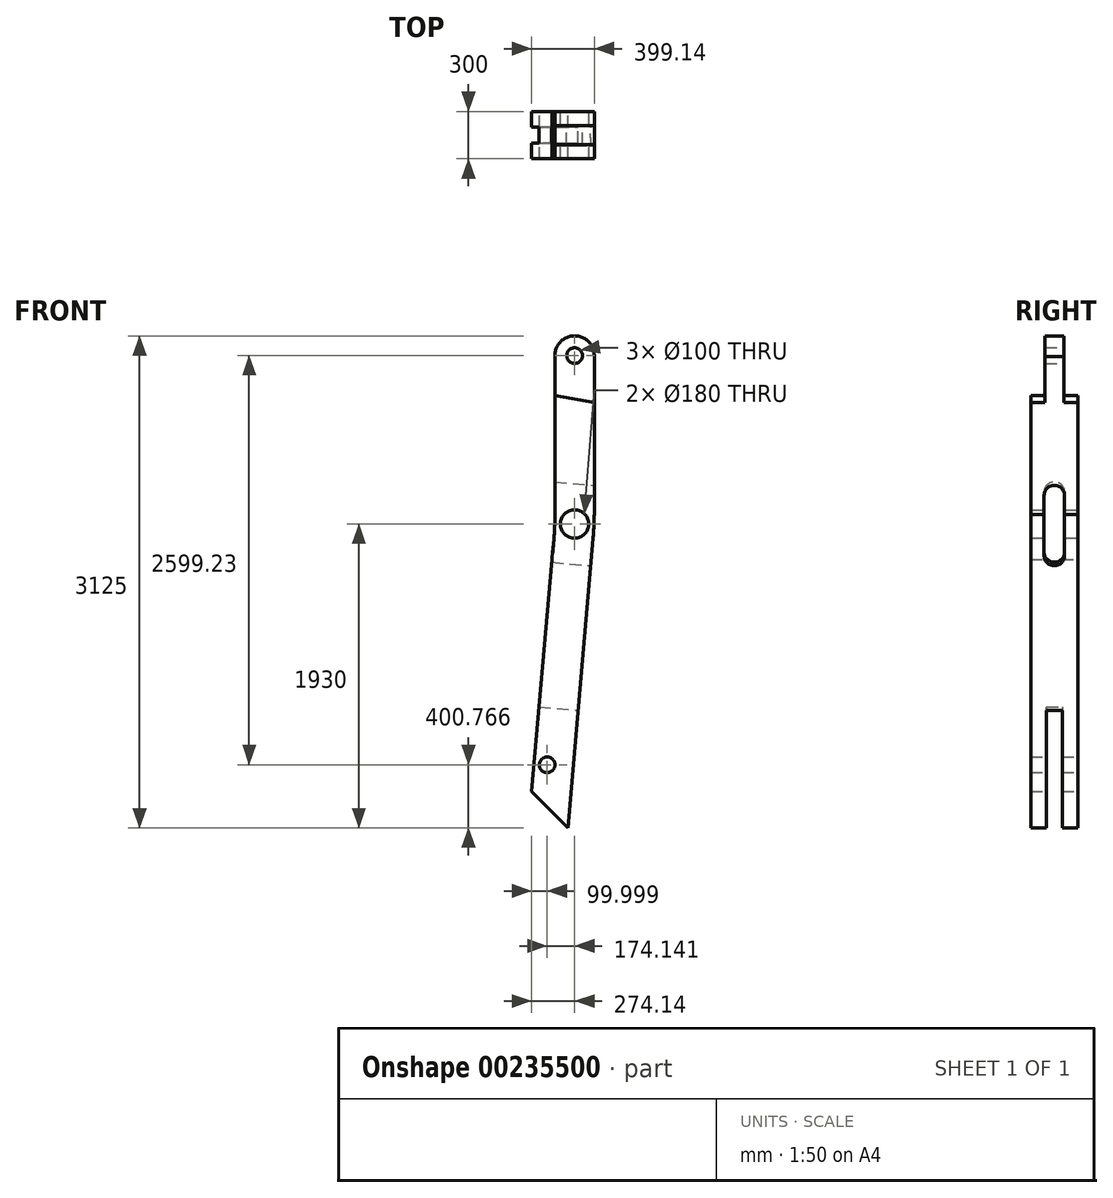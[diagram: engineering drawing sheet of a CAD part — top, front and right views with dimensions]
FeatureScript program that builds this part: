
annotation { "Feature Type Name" : "Feature", "Feature Type Description" : "" }
export const myFeature = defineFeature(function(context is Context, id is Id, definition is map)
    precondition{}
    {
        {
            var Q0;
            Q0=qCreatedBy(makeId("Front.planeOp"),FACE);
            var sketch = newSketch(context, id + "F0", { "sketchPlane" : qUnion([Q0])});
            skLineSegment(sketch, "E0", {"start": v(0, 1070) * mm, "end": v(0, 0) * mm, "construction": true});
            skLineSegment(sketch, "E1", {"start": v(0, 0) * mm, "end": v(-158.76, -1814.62) * mm, "construction": true});
            skLineSegment(sketch, "E2", {"start": v(-124.82, 1070) * mm, "end": v(-124.82, 60) * mm});
            skLineSegment(sketch, "E3", {"start": v(124.82, 1070) * mm, "end": v(124.82, 60) * mm});
            skLineSegment(sketch, "E4", {"start": v(-145.05, -223.74) * mm, "end": v(-274.14, -1699.23) * mm});
            skArc(sketch, "E5", {"start": v(-145.05, -223.74) * mm, "mid": v(-129.89, -82.23) * mm, "end": v(-124.82, 60) * mm});
            skArc(sketch, "E6", {"start": v(117.32, -93.2) * mm, "mid": v(122.54, -16.67) * mm, "end": v(124.82, 60) * mm});
            skLineSegment(sketch, "E7", {"start": v(117.32, -93.2) * mm, "end": v(-43.38, -1930) * mm});
            skLineSegment(sketch, "E8", {"start": v(-43.38, -1930) * mm, "end": v(-274.14, -1699.23) * mm});
            skLineSegment(sketch, "E9", {"start": v(-43.38, -1930) * mm, "end": v(-861.48, -1930) * mm, "construction": true});
            skCircle(sketch, "E10", {"center": v(0, 0) * mm, "radius": 90 * mm});
            skCircle(sketch, "E11", {"center": v(-174.14, -1529.23) * mm, "radius": 50 * mm});
            skLineSegment(sketch, "E12", {"start": v(124.82, 1070) * mm, "end": v(-124.82, 1070) * mm, "construction": true});
            skArc(sketch, "E13", {"start": v(124.82, 1063.35) * mm, "mid": v(0, 1195) * mm, "end": v(-124.82, 1063.35) * mm});
            skPoint(sketch, "E14", {"position": v(0, 1195) * mm});
            skLineSegment(sketch, "E15", {"start": v(-124.82, 815) * mm, "end": v(124.82, 770.98) * mm});
            skCircle(sketch, "E16", {"center": v(0, 1070) * mm, "radius": 50 * mm});
            skSolve(sketch);
        }
        {
            var Q0;
            Q0=makeQuery(id+"F0.imprint","IMPRINT",FACE,{"disambiguationData":[TD([[makeQuery(id+"F0.imprint","IMPRINT",EDGE,{"derivedFrom":sQuery(id+"F0.wireOp",EDGE,"E4")}),1.0]])]});
            extrude(context, id + "F1", {"entities" : qUnion([Q0]), "endBound" : BoundingType.SYMMETRIC, "depth" : 300 * mm});
        }
        {
            var Q0;
            {var subQ1=sQuery(id+"F0.wireOp",EDGE,"E13");Q0=makeQuery(id+"F0.imprint","IMPRINT",FACE,{"disambiguationData":[TD([[makeQuery(id+"F0.imprint","IMPRINT",EDGE,{"derivedFrom":subQ1}),1.0]])]});}
            extrude(context, id + "F2", {"entities" : qUnion([Q0]), "operationType" : NewBodyOperationType.ADD, "endBound" : BoundingType.SYMMETRIC, "depth" : 120 * mm});
        }
        {
            var Q0;
            Q0=makeQuery(id+"F1.opExtrude","SWEPT_FACE",FACE,{"disambiguationData":[OSD([sQuery(id+"F0.wireOp",EDGE,"E7")])]});
            var sketch = newSketch(context, id + "F3", { "sketchPlane" : qUnion([Q0])});
            skLineSegment(sketch, "E17", {"start": v(-60, 1190.93) * mm, "end": v(60, 1190.93) * mm});
            skLineSegment(sketch, "E18.0", {"start": v(0, 1076.8) * mm, "end": v(0, 70.65) * mm, "construction": true});
            skArc(sketch, "E19", {"start": v(65, 190.45) * mm, "mid": v(0, 255.45) * mm, "end": v(-65, 190.45) * mm});
            skArc(sketch, "E20", {"start": v(-65, -189.55) * mm, "mid": v(0, -254.55) * mm, "end": v(65, -189.55) * mm});
            skLineSegment(sketch, "E21", {"start": v(-116.59, -189.55) * mm, "end": v(118.95, -189.55) * mm, "construction": true});
            skLineSegment(sketch, "E22", {"start": v(-119.53, 190.45) * mm, "end": v(133.67, 190.45) * mm, "construction": true});
            skLineSegment(sketch, "E23", {"start": v(-65, 190.45) * mm, "end": v(-65, -189.55) * mm});
            skLineSegment(sketch, "E24", {"start": v(65, 190.45) * mm, "end": v(65, -189.55) * mm});
            skLineSegment(sketch, "E25.0", {"start": v(0, -90) * mm, "end": v(0, 90) * mm, "construction": true});
            skLineSegment(sketch, "E26.0", {"start": v(0, -82.62) * mm, "end": v(0, -1926.44) * mm, "construction": true});
            skLineSegment(sketch, "E27", {"start": v(-50, -1926.44) * mm, "end": v(-50, -1176.44) * mm});
            skLineSegment(sketch, "E28", {"start": v(-50, -1176.44) * mm, "end": v(50, -1176.44) * mm});
            skLineSegment(sketch, "E29", {"start": v(50, -1176.44) * mm, "end": v(50, -1926.44) * mm});
            skLineSegment(sketch, "E30.0", {"start": v(-50, -1926.44) * mm, "end": v(50, -1926.44) * mm});
            skPoint(sketch, "E31.orphan", {"position": v(-150, -1926.44) * mm});
            skPoint(sketch, "E32.orphan", {"position": v(150, -1926.44) * mm});
            skSolve(sketch);
        }
        {
            var Q0;
            {var subQ0=sQuery(id+"F3.wireOp",EDGE,"E19");Q0=makeQuery(id+"F3.imprint","IMPRINT",FACE,{"disambiguationData":[TD([[makeQuery(id+"F3.imprint","IMPRINT",EDGE,{"derivedFrom":subQ0}),1.0]])]});}
            var Q1;
            {var subQ0=sQuery(id+"F3.wireOp",EDGE,"E20");Q1=makeQuery(id+"F3.imprint","IMPRINT",FACE,{"disambiguationData":[TD([[makeQuery(id+"F3.imprint","IMPRINT",EDGE,{"derivedFrom":subQ0}),1.0]])]});}
            var Q2;
            Q2=makeQuery(id+"F3.imprint","IMPRINT",FACE,{"disambiguationData":[TD([[makeQuery(id+"F3.imprint","IMPRINT",EDGE,{"derivedFrom":sQuery(id+"F3.wireOp",EDGE,"E27")}),-1.0]])]});
            extrude(context, id + "F4", {"entities" : qUnion([Q0, Q1, Q2]), "operationType" : NewBodyOperationType.REMOVE, "endBound" : BoundingType.THROUGH_ALL, "oppositeDirection" : true, "depth" : 25 * mm});
        }
    });
